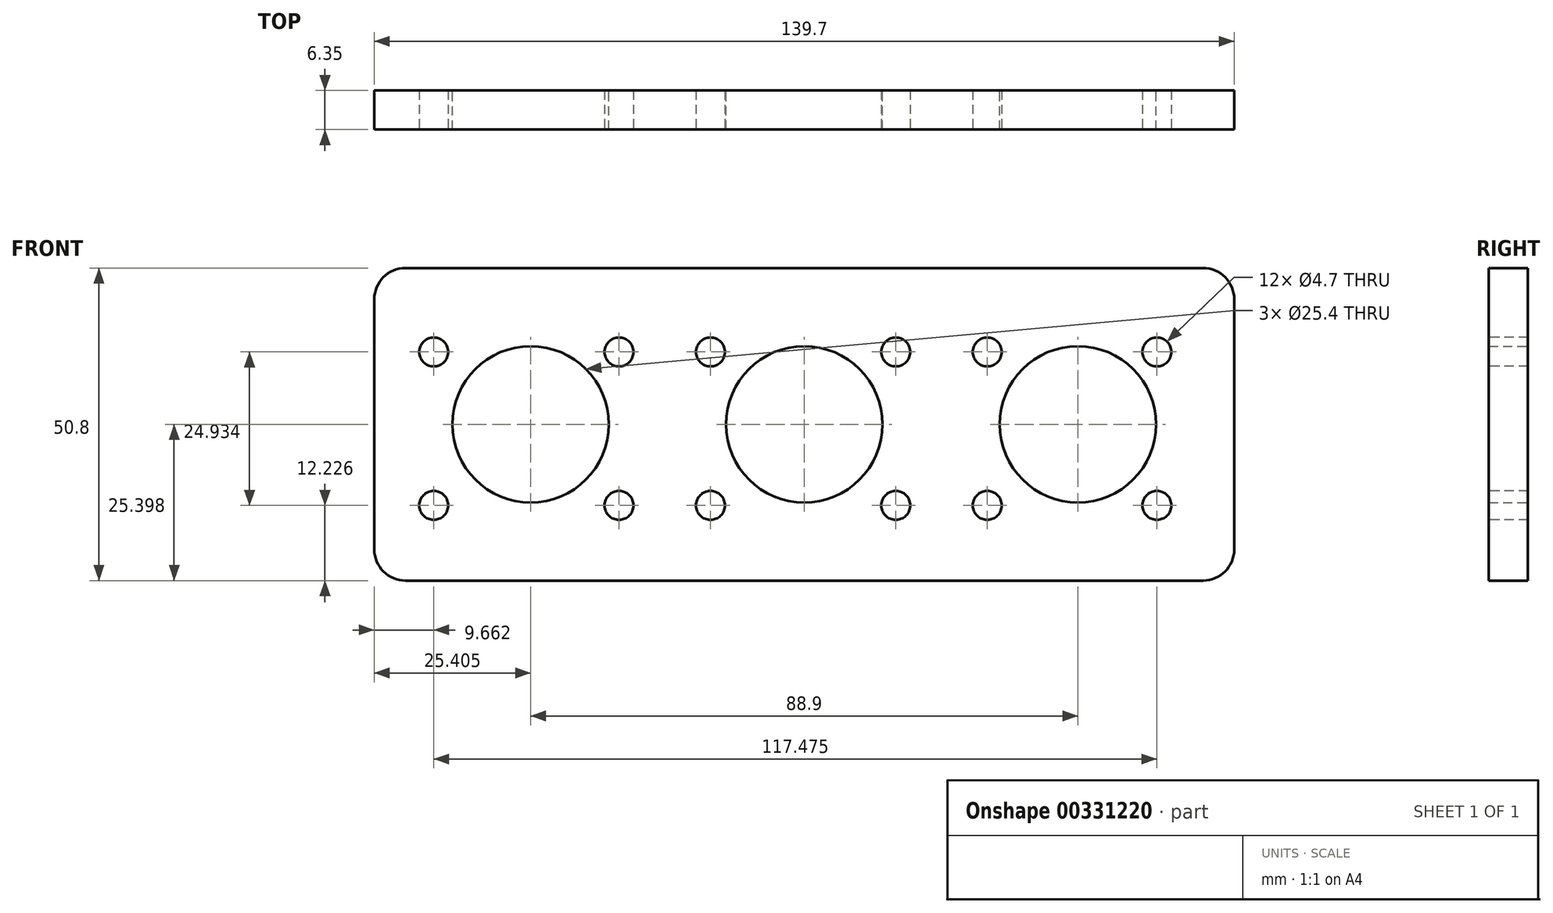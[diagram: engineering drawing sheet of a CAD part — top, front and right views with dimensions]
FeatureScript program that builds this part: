
annotation { "Feature Type Name" : "Feature", "Feature Type Description" : "" }
export const myFeature = defineFeature(function(context is Context, id is Id, definition is map)
    precondition{}
    {
        {
            var Q0;
            Q0=qCreatedBy(makeId("Front.planeOp"),FACE);
            var sketch = newSketch(context, id + "F0", { "sketchPlane" : qUnion([Q0])});
            skLineSegment(sketch, "E0.bottom", {"start": v(-73.24, 13.64) * mm, "end": v(66.46, 13.64) * mm});
            skLineSegment(sketch, "E0.top", {"start": v(-73.24, -37.16) * mm, "end": v(66.46, -37.16) * mm});
            skLineSegment(sketch, "E0.left", {"start": v(-73.24, 13.64) * mm, "end": v(-73.24, -37.16) * mm});
            skLineSegment(sketch, "E0.right", {"start": v(66.46, 13.64) * mm, "end": v(66.46, -37.16) * mm});
            skCircle(sketch, "E1", {"center": v(-47.84, -11.76) * mm, "radius": 12.7 * mm});
            skCircle(sketch, "E2", {"center": v(-3.39, -11.76) * mm, "radius": 12.7 * mm});
            skCircle(sketch, "E3", {"center": v(41.06, -11.76) * mm, "radius": 12.7 * mm});
            skCircle(sketch, "E4", {"center": v(-47.84, -11.76) * mm, "radius": 10.16 * mm, "construction": true});
            skCircle(sketch, "E5", {"center": v(-3.39, -11.76) * mm, "radius": 10.16 * mm, "construction": true});
            skCircle(sketch, "E6", {"center": v(41.06, -11.76) * mm, "radius": 10.16 * mm, "construction": true});
            skSolve(sketch);
        }
        {
            var Q0;
            Q0=makeQuery(id+"F0.imprint","IMPRINT",FACE,{"disambiguationData":[TD([[makeQuery(id+"F0.imprint","IMPRINT",EDGE,{"derivedFrom":sQuery(id+"F0.wireOp",EDGE,"E0.bottom")}),-1.0]])]});
            extrude(context, id + "F1", {"entities" : qUnion([Q0]), "depth" : 6.35 * mm});
        }
        {
            var Q0;
            Q0=makeQuery(id+"F1.opExtrude","SWEPT_EDGE",EDGE,{"disambiguationData":[OSD([sQuery(id+"F0.wireOp",EDGE,"E0.bottom"),sQuery(id+"F0.wireOp",EDGE,"E0.left")])]});
            var Q1;
            Q1=makeQuery(id+"F1.opExtrude","SWEPT_EDGE",EDGE,{"disambiguationData":[OSD([sQuery(id+"F0.wireOp",EDGE,"E0.bottom"),sQuery(id+"F0.wireOp",EDGE,"E0.right")])]});
            var Q2;
            Q2=makeQuery(id+"F1.opExtrude","SWEPT_EDGE",EDGE,{"disambiguationData":[OSD([sQuery(id+"F0.wireOp",EDGE,"E0.top"),sQuery(id+"F0.wireOp",EDGE,"E0.right")])]});
            var Q3;
            Q3=makeQuery(id+"F1.opExtrude","SWEPT_EDGE",EDGE,{"disambiguationData":[OSD([sQuery(id+"F0.wireOp",EDGE,"E0.top"),sQuery(id+"F0.wireOp",EDGE,"E0.left")])]});
            fillet(context, id + "F2", {"entities" : qUnion([Q0, Q1, Q2, Q3]), "radius" : 5.08 * mm, "tangentPropagation" : true, "allowEdgeOverflow" : false});
        }
        {
            var Q0;
            Q0=makeQuery(id+"F1.opExtrude","CAP_FACE",FACE,{"disambiguationData":[OSD([sQuery(id+"F0.wireOp",EDGE,"E0.bottom"),sQuery(id+"F0.wireOp",EDGE,"E0.top"),sQuery(id+"F0.wireOp",EDGE,"E0.left"),sQuery(id+"F0.wireOp",EDGE,"E0.right"),sQuery(id+"F0.wireOp",EDGE,"E1"),sQuery(id+"F0.wireOp",EDGE,"E2"),sQuery(id+"F0.wireOp",EDGE,"E3")])],"isStart":false});
            var sketch = newSketch(context, id + "F3", { "sketchPlane" : qUnion([Q0])});
            skCircle(sketch, "E7", {"center": v(-63.58, 0) * mm, "radius": 2.35 * mm});
            skCircle(sketch, "E8", {"center": v(-33.48, 0) * mm, "radius": 2.35 * mm});
            skCircle(sketch, "E9", {"center": v(-63.58, -24.93) * mm, "radius": 2.35 * mm});
            skCircle(sketch, "E10", {"center": v(-33.48, -24.93) * mm, "radius": 2.35 * mm});
            skCircle(sketch, "E11", {"center": v(-18.62, 0) * mm, "radius": 2.35 * mm});
            skCircle(sketch, "E12", {"center": v(11.48, 0) * mm, "radius": 2.35 * mm});
            skCircle(sketch, "E13", {"center": v(-18.62, -24.93) * mm, "radius": 2.35 * mm});
            skCircle(sketch, "E14", {"center": v(11.48, -24.93) * mm, "radius": 2.35 * mm});
            skCircle(sketch, "E15", {"center": v(26.34, 0) * mm, "radius": 2.35 * mm});
            skCircle(sketch, "E16", {"center": v(53.9, 0) * mm, "radius": 2.35 * mm});
            skCircle(sketch, "E17", {"center": v(26.34, -24.93) * mm, "radius": 2.35 * mm});
            skCircle(sketch, "E18", {"center": v(53.9, -24.93) * mm, "radius": 2.35 * mm});
            skLineSegment(sketch, "E19", {"start": v(-73.24, 0) * mm, "end": v(62.68, 0) * mm, "construction": true});
            skLineSegment(sketch, "E20", {"start": v(-73.24, -24.93) * mm, "end": v(66.46, -24.93) * mm, "construction": true});
            skSolve(sketch);
        }
        {
            var Q0;
            Q0 = qSketchRegion(id + "F3", true);
            extrude(context, id + "F4", {"entities" : qUnion([Q0]), "operationType" : NewBodyOperationType.REMOVE, "oppositeDirection" : true, "depth" : 25.4 * mm, "hasSecondDirection" : true, "secondDirectionOppositeDirection" : false, "secondDirectionDepth" : 25.4 * mm});
        }
    });
